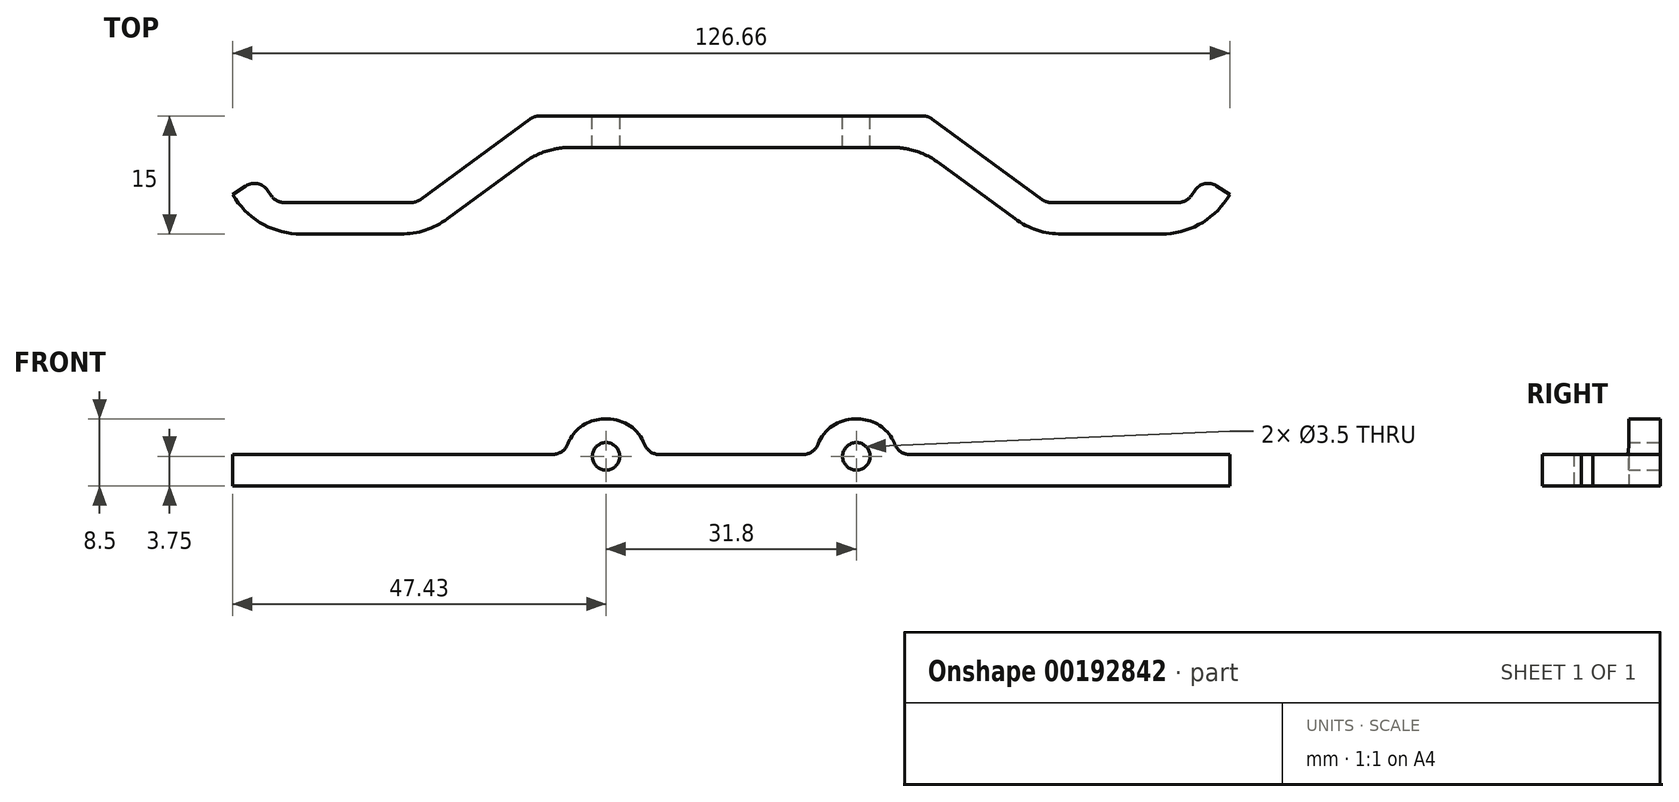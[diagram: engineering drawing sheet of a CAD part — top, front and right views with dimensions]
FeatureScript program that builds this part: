
annotation { "Feature Type Name" : "Feature", "Feature Type Description" : "" }
export const myFeature = defineFeature(function(context is Context, id is Id, definition is map)
    precondition{}
    {
        {
            var Q0;
            Q0=qCreatedBy(makeId("Top.planeOp"),FACE);
            var sketch = newSketch(context, id + "F0", { "sketchPlane" : qUnion([Q0])});
            skLineSegment(sketch, "E0", {"start": v(-85, -7.79) * mm, "end": v(-82.86, -11) * mm});
            skLineSegment(sketch, "E1", {"start": v(-82.86, -11) * mm, "end": v(-65, -11) * mm});
            skLineSegment(sketch, "E2", {"start": v(-65, -11) * mm, "end": v(-50, 0) * mm});
            skLineSegment(sketch, "E3", {"start": v(-50, 0) * mm, "end": v(0, 0) * mm});
            skLineSegment(sketch, "E4", {"start": v(0, 0) * mm, "end": v(15, -11) * mm});
            skLineSegment(sketch, "E5", {"start": v(15, -11) * mm, "end": v(32.86, -11) * mm});
            skLineSegment(sketch, "E6", {"start": v(32.86, -11) * mm, "end": v(35, -7.79) * mm});
            skLineSegment(sketch, "E7", {"start": v(35, -7.79) * mm, "end": v(38.33, -10) * mm});
            skLineSegment(sketch, "E8", {"start": v(38.33, -10) * mm, "end": v(35, -15) * mm});
            skLineSegment(sketch, "E9", {"start": v(35, -15) * mm, "end": v(13.7, -15) * mm});
            skLineSegment(sketch, "E10", {"start": v(13.7, -15) * mm, "end": v(-1.3, -4) * mm});
            skLineSegment(sketch, "E11", {"start": v(-1.3, -4) * mm, "end": v(-48.7, -4) * mm});
            skLineSegment(sketch, "E12", {"start": v(-48.7, -4) * mm, "end": v(-63.7, -15) * mm});
            skLineSegment(sketch, "E13", {"start": v(-63.7, -15) * mm, "end": v(-85, -15) * mm});
            skLineSegment(sketch, "E14", {"start": v(-85, -15) * mm, "end": v(-88.33, -10) * mm});
            skLineSegment(sketch, "E15", {"start": v(-88.33, -10) * mm, "end": v(-85, -7.79) * mm});
            skSolve(sketch);
        }
        {
            var Q0;
            Q0 = qSketchRegion(id + "F0", true);
            extrude(context, id + "F1", {"entities" : qUnion([Q0]), "depth" : 4 * mm});
        }
        {
            var Q0;
            Q0=makeQuery(id+"F1.opExtrude","SWEPT_FACE",FACE,{"disambiguationData":[OSD([sQuery(id+"F0.wireOp",EDGE,"E3")])]});
            var sketch = newSketch(context, id + "F2", { "sketchPlane" : qUnion([Q0])});
            skPoint(sketch, "E16", {"position": v(9.1, 3.75) * mm});
            skPoint(sketch, "E17", {"position": v(40.9, 3.75) * mm});
            skCircle(sketch, "E18", {"center": v(40.9, 3.75) * mm, "radius": 1.75 * mm, "construction": true});
            skCircle(sketch, "E19", {"center": v(9.1, 3.75) * mm, "radius": 1.75 * mm, "construction": true});
            skLineSegment(sketch, "E20.bottom", {"start": v(13.85, 8.5) * mm, "end": v(4.35, 8.5) * mm});
            skLineSegment(sketch, "E20.top", {"start": v(13.85, 0) * mm, "end": v(4.35, 0) * mm});
            skLineSegment(sketch, "E20.left", {"start": v(13.85, 8.5) * mm, "end": v(13.85, 0) * mm});
            skLineSegment(sketch, "E20.right", {"start": v(4.35, 8.5) * mm, "end": v(4.35, 0) * mm});
            skLineSegment(sketch, "E21.bottom", {"start": v(36.15, 8.5) * mm, "end": v(45.65, 8.5) * mm});
            skLineSegment(sketch, "E21.top", {"start": v(36.15, 0) * mm, "end": v(45.65, 0) * mm});
            skLineSegment(sketch, "E21.left", {"start": v(36.15, 8.5) * mm, "end": v(36.15, 0) * mm});
            skLineSegment(sketch, "E21.right", {"start": v(45.65, 8.5) * mm, "end": v(45.65, 0) * mm});
            skLineSegment(sketch, "E22", {"start": v(9.1, 3.75) * mm, "end": v(40.9, 3.75) * mm, "construction": true});
            skPoint(sketch, "E23", {"position": v(25, 3.75) * mm});
            skSolve(sketch);
        }
        {
            var Q0;
            Q0 = qSketchRegion(id + "F2", true);
            var Q1;
            Q1=makeQuery(id+"F1.opExtrude","SWEPT_FACE",FACE,{"disambiguationData":[OSD([sQuery(id+"F0.wireOp",EDGE,"E11")])]});
            extrude(context, id + "F3", {"entities" : qUnion([Q0]), "operationType" : NewBodyOperationType.ADD, "endBound" : BoundingType.UP_TO_SURFACE, "oppositeDirection" : true, "endBoundEntityFace" : qUnion([Q1]), "depth" : 25 * mm});
        }
        {
            var Q0;
            Q0=makeQuery(id+"F3.boolean.opBoolean","MERGE",FACE,{"derivedFrom":[makeQuery(id+"F1.opExtrude","SWEPT_FACE",FACE,{"disambiguationData":[OSD([sQuery(id+"F0.wireOp",EDGE,"E3")])]}),makeQuery(id+"F3.opExtrude","CAP_FACE",FACE,{"disambiguationData":[OSD([sQuery(id+"F2.wireOp",EDGE,"E20.bottom"),sQuery(id+"F2.wireOp",EDGE,"E20.top"),sQuery(id+"F2.wireOp",EDGE,"E20.left"),sQuery(id+"F2.wireOp",EDGE,"E20.right")])],"isStart":true}),makeQuery(id+"F3.opExtrude","CAP_FACE",FACE,{"disambiguationData":[OSD([sQuery(id+"F2.wireOp",EDGE,"E21.bottom"),sQuery(id+"F2.wireOp",EDGE,"E21.top"),sQuery(id+"F2.wireOp",EDGE,"E21.left"),sQuery(id+"F2.wireOp",EDGE,"E21.right")])],"isStart":true})]});
            var sketch = newSketch(context, id + "F4", { "sketchPlane" : qUnion([Q0])});
            skCircle(sketch, "E24", {"center": v(9.1, 3.75) * mm, "radius": 1.75 * mm});
            skCircle(sketch, "E25", {"center": v(40.9, 3.75) * mm, "radius": 1.75 * mm});
            skSolve(sketch);
        }
        {
            var Q0;
            Q0 = qSketchRegion(id + "F4", true);
            var Q1;
            {var subQ0=sQuery(id+"F0.wireOp",EDGE,"E11");Q1=makeQuery(id+"F3.boolean.opBoolean","MERGE",FACE,{"derivedFrom":[makeQuery(id+"F1.opExtrude","SWEPT_FACE",FACE,{"disambiguationData":[OSD([subQ0])]}),makeQuery(id+"F3.opExtrude","CAP_FACE",FACE,{"disambiguationData":[OSD([subQ0]),ownerDisambiguation([makeQuery(id+"F3.opExtrude","SWEPT_BODY",BODY,{"disambiguationData":[OSD([sQuery(id+"F2.wireOp",EDGE,"E20.bottom"),sQuery(id+"F2.wireOp",EDGE,"E20.top"),sQuery(id+"F2.wireOp",EDGE,"E20.left"),sQuery(id+"F2.wireOp",EDGE,"E20.right")])]})])],"isStart":false}),makeQuery(id+"F3.opExtrude","CAP_FACE",FACE,{"disambiguationData":[OSD([subQ0]),ownerDisambiguation([makeQuery(id+"F3.opExtrude","SWEPT_BODY",BODY,{"disambiguationData":[OSD([sQuery(id+"F2.wireOp",EDGE,"E21.bottom"),sQuery(id+"F2.wireOp",EDGE,"E21.top"),sQuery(id+"F2.wireOp",EDGE,"E21.left"),sQuery(id+"F2.wireOp",EDGE,"E21.right")])]})])],"isStart":false})]});}
            extrude(context, id + "F5", {"entities" : qUnion([Q0]), "operationType" : NewBodyOperationType.REMOVE, "endBound" : BoundingType.UP_TO_SURFACE, "oppositeDirection" : true, "endBoundEntityFace" : qUnion([Q1]), "depth" : 25 * mm});
        }
        {
            var Q0;
            Q0=makeQuery(id+"F1.opExtrude","SWEPT_EDGE",EDGE,{"disambiguationData":[OSD([sQuery(id+"F0.wireOp",EDGE,"E8"),sQuery(id+"F0.wireOp",EDGE,"E9")])]});
            var Q1;
            Q1=makeQuery(id+"F1.opExtrude","SWEPT_EDGE",EDGE,{"disambiguationData":[OSD([sQuery(id+"F0.wireOp",EDGE,"E9"),sQuery(id+"F0.wireOp",EDGE,"E10")])]});
            var Q2;
            Q2=makeQuery(id+"F1.opExtrude","SWEPT_EDGE",EDGE,{"disambiguationData":[OSD([sQuery(id+"F0.wireOp",EDGE,"E12"),sQuery(id+"F0.wireOp",EDGE,"E13")])]});
            var Q3;
            Q3=makeQuery(id+"F1.opExtrude","SWEPT_EDGE",EDGE,{"disambiguationData":[OSD([sQuery(id+"F0.wireOp",EDGE,"E13"),sQuery(id+"F0.wireOp",EDGE,"E14")])]});
            var Q4;
            Q4=makeQuery(id+"F1.opExtrude","SWEPT_EDGE",EDGE,{"disambiguationData":[OSD([sQuery(id+"F0.wireOp",EDGE,"E11"),sQuery(id+"F0.wireOp",EDGE,"E12")])]});
            var Q5;
            Q5=makeQuery(id+"F1.opExtrude","SWEPT_EDGE",EDGE,{"disambiguationData":[OSD([sQuery(id+"F0.wireOp",EDGE,"E10"),sQuery(id+"F0.wireOp",EDGE,"E11")])]});
            fillet(context, id + "F6", {"entities" : qUnion([Q0, Q1, Q2, Q3, Q4, Q5]), "radius" : 10 * mm, "tangentPropagation" : true, "allowEdgeOverflow" : false});
        }
        {
            var Q0;
            Q0=makeQuery(id+"F1.opExtrude","SWEPT_EDGE",EDGE,{"disambiguationData":[OSD([sQuery(id+"F0.wireOp",EDGE,"E6"),sQuery(id+"F0.wireOp",EDGE,"E7")])]});
            var Q1;
            Q1=makeQuery(id+"F1.opExtrude","SWEPT_EDGE",EDGE,{"disambiguationData":[OSD([sQuery(id+"F0.wireOp",EDGE,"E0"),sQuery(id+"F0.wireOp",EDGE,"E15")])]});
            var Q2;
            Q2=makeQuery(id+"F1.opExtrude","SWEPT_EDGE",EDGE,{"disambiguationData":[OSD([sQuery(id+"F0.wireOp",EDGE,"E1"),sQuery(id+"F0.wireOp",EDGE,"E2")])]});
            var Q3;
            Q3=makeQuery(id+"F1.opExtrude","SWEPT_EDGE",EDGE,{"disambiguationData":[OSD([sQuery(id+"F0.wireOp",EDGE,"E0"),sQuery(id+"F0.wireOp",EDGE,"E1")])]});
            var Q4;
            Q4=makeQuery(id+"F1.opExtrude","SWEPT_EDGE",EDGE,{"disambiguationData":[OSD([sQuery(id+"F0.wireOp",EDGE,"E5"),sQuery(id+"F0.wireOp",EDGE,"E6")])]});
            var Q5;
            Q5=makeQuery(id+"F1.opExtrude","SWEPT_EDGE",EDGE,{"disambiguationData":[OSD([sQuery(id+"F0.wireOp",EDGE,"E4"),sQuery(id+"F0.wireOp",EDGE,"E5")])]});
            var Q6;
            Q6=makeQuery(id+"F1.opExtrude","SWEPT_EDGE",EDGE,{"disambiguationData":[OSD([sQuery(id+"F0.wireOp",EDGE,"E3"),sQuery(id+"F0.wireOp",EDGE,"E4")])]});
            var Q7;
            Q7=makeQuery(id+"F1.opExtrude","SWEPT_EDGE",EDGE,{"disambiguationData":[OSD([sQuery(id+"F0.wireOp",EDGE,"E2"),sQuery(id+"F0.wireOp",EDGE,"E3")])]});
            fillet(context, id + "F7", {"entities" : qUnion([Q0, Q1, Q2, Q3, Q4, Q5, Q6, Q7]), "radius" : 2 * mm, "tangentPropagation" : true, "allowEdgeOverflow" : false});
        }
        {
            var Q0;
            Q0=makeQuery(id+"F3.boolean.opBoolean","INTERSECT",EDGE,{"derivedFrom":[makeQuery(id+"F1.opExtrude","CAP_FACE",FACE,{"disambiguationData":[OSD([sQuery(id+"F0.wireOp",EDGE,"E0"),sQuery(id+"F0.wireOp",EDGE,"E1"),sQuery(id+"F0.wireOp",EDGE,"E2"),sQuery(id+"F0.wireOp",EDGE,"E3"),sQuery(id+"F0.wireOp",EDGE,"E4"),sQuery(id+"F0.wireOp",EDGE,"E5"),sQuery(id+"F0.wireOp",EDGE,"E6"),sQuery(id+"F0.wireOp",EDGE,"E7"),sQuery(id+"F0.wireOp",EDGE,"E8"),sQuery(id+"F0.wireOp",EDGE,"E9"),sQuery(id+"F0.wireOp",EDGE,"E10"),sQuery(id+"F0.wireOp",EDGE,"E11"),sQuery(id+"F0.wireOp",EDGE,"E12"),sQuery(id+"F0.wireOp",EDGE,"E13"),sQuery(id+"F0.wireOp",EDGE,"E14"),sQuery(id+"F0.wireOp",EDGE,"E15")])],"isStart":false}),makeQuery(id+"F3.opExtrude","SWEPT_FACE",FACE,{"disambiguationData":[OSD([sQuery(id+"F2.wireOp",EDGE,"E21.right")])]})]});
            var Q1;
            Q1=makeQuery(id+"F3.boolean.opBoolean","INTERSECT",EDGE,{"derivedFrom":[makeQuery(id+"F1.opExtrude","CAP_FACE",FACE,{"disambiguationData":[OSD([sQuery(id+"F0.wireOp",EDGE,"E0"),sQuery(id+"F0.wireOp",EDGE,"E1"),sQuery(id+"F0.wireOp",EDGE,"E2"),sQuery(id+"F0.wireOp",EDGE,"E3"),sQuery(id+"F0.wireOp",EDGE,"E4"),sQuery(id+"F0.wireOp",EDGE,"E5"),sQuery(id+"F0.wireOp",EDGE,"E6"),sQuery(id+"F0.wireOp",EDGE,"E7"),sQuery(id+"F0.wireOp",EDGE,"E8"),sQuery(id+"F0.wireOp",EDGE,"E9"),sQuery(id+"F0.wireOp",EDGE,"E10"),sQuery(id+"F0.wireOp",EDGE,"E11"),sQuery(id+"F0.wireOp",EDGE,"E12"),sQuery(id+"F0.wireOp",EDGE,"E13"),sQuery(id+"F0.wireOp",EDGE,"E14"),sQuery(id+"F0.wireOp",EDGE,"E15")])],"isStart":false}),makeQuery(id+"F3.opExtrude","SWEPT_FACE",FACE,{"disambiguationData":[OSD([sQuery(id+"F2.wireOp",EDGE,"E20.left")])]})]});
            var Q2;
            Q2=makeQuery(id+"F3.boolean.opBoolean","INTERSECT",EDGE,{"derivedFrom":[makeQuery(id+"F1.opExtrude","CAP_FACE",FACE,{"disambiguationData":[OSD([sQuery(id+"F0.wireOp",EDGE,"E0"),sQuery(id+"F0.wireOp",EDGE,"E1"),sQuery(id+"F0.wireOp",EDGE,"E2"),sQuery(id+"F0.wireOp",EDGE,"E3"),sQuery(id+"F0.wireOp",EDGE,"E4"),sQuery(id+"F0.wireOp",EDGE,"E5"),sQuery(id+"F0.wireOp",EDGE,"E6"),sQuery(id+"F0.wireOp",EDGE,"E7"),sQuery(id+"F0.wireOp",EDGE,"E8"),sQuery(id+"F0.wireOp",EDGE,"E9"),sQuery(id+"F0.wireOp",EDGE,"E10"),sQuery(id+"F0.wireOp",EDGE,"E11"),sQuery(id+"F0.wireOp",EDGE,"E12"),sQuery(id+"F0.wireOp",EDGE,"E13"),sQuery(id+"F0.wireOp",EDGE,"E14"),sQuery(id+"F0.wireOp",EDGE,"E15")])],"isStart":false}),makeQuery(id+"F3.opExtrude","SWEPT_FACE",FACE,{"disambiguationData":[OSD([sQuery(id+"F2.wireOp",EDGE,"E20.right")])]})]});
            var Q3;
            Q3=makeQuery(id+"F3.boolean.opBoolean","INTERSECT",EDGE,{"derivedFrom":[makeQuery(id+"F1.opExtrude","CAP_FACE",FACE,{"disambiguationData":[OSD([sQuery(id+"F0.wireOp",EDGE,"E0"),sQuery(id+"F0.wireOp",EDGE,"E1"),sQuery(id+"F0.wireOp",EDGE,"E2"),sQuery(id+"F0.wireOp",EDGE,"E3"),sQuery(id+"F0.wireOp",EDGE,"E4"),sQuery(id+"F0.wireOp",EDGE,"E5"),sQuery(id+"F0.wireOp",EDGE,"E6"),sQuery(id+"F0.wireOp",EDGE,"E7"),sQuery(id+"F0.wireOp",EDGE,"E8"),sQuery(id+"F0.wireOp",EDGE,"E9"),sQuery(id+"F0.wireOp",EDGE,"E10"),sQuery(id+"F0.wireOp",EDGE,"E11"),sQuery(id+"F0.wireOp",EDGE,"E12"),sQuery(id+"F0.wireOp",EDGE,"E13"),sQuery(id+"F0.wireOp",EDGE,"E14"),sQuery(id+"F0.wireOp",EDGE,"E15")])],"isStart":false}),makeQuery(id+"F3.opExtrude","SWEPT_FACE",FACE,{"disambiguationData":[OSD([sQuery(id+"F2.wireOp",EDGE,"E21.left")])]})]});
            fillet(context, id + "F8", {"entities" : qUnion([Q0, Q1, Q2, Q3]), "radius" : 2 * mm, "tangentPropagation" : true, "allowEdgeOverflow" : false});
        }
        {
            var Q0;
            Q0=makeQuery(id+"F3.opExtrude","SWEPT_EDGE",EDGE,{"disambiguationData":[OSD([sQuery(id+"F2.wireOp",EDGE,"E21.bottom"),sQuery(id+"F2.wireOp",EDGE,"E21.right")])]});
            var Q1;
            Q1=makeQuery(id+"F3.opExtrude","SWEPT_EDGE",EDGE,{"disambiguationData":[OSD([sQuery(id+"F2.wireOp",EDGE,"E21.bottom"),sQuery(id+"F2.wireOp",EDGE,"E21.left")])]});
            var Q2;
            Q2=makeQuery(id+"F3.opExtrude","SWEPT_EDGE",EDGE,{"disambiguationData":[OSD([sQuery(id+"F2.wireOp",EDGE,"E20.bottom"),sQuery(id+"F2.wireOp",EDGE,"E20.left")])]});
            var Q3;
            Q3=makeQuery(id+"F3.opExtrude","SWEPT_EDGE",EDGE,{"disambiguationData":[OSD([sQuery(id+"F2.wireOp",EDGE,"E20.bottom"),sQuery(id+"F2.wireOp",EDGE,"E20.right")])]});
            fillet(context, id + "F9", {"entities" : qUnion([Q0, Q1, Q2, Q3]), "radius" : 5 * mm, "tangentPropagation" : true, "allowEdgeOverflow" : false});
        }
    });
